# Revit family: Indoor_Pendant Lamp_Santa&Cole_La Colilla
name_source: partatom
category: Luminarias
revit_build: Autodesk Revit 2018 (Build: 20190510_1515(x64)
units: mm (PartAtom-declared; Revit-internal decimal feet)

## family parameters
Anfitrión = Cara
Compartido = No
Corte con vacíos al cargar = No
Cota de conector redondo = Diámetro de uso
Origen de luz = Sí
Punto de cálculo de habitación = No
Tipo de pieza = Normal

## types (2) — shared parameters
Assembly Instructions - CE = https://www.santacole.com
Cambio de temperatura de color de luz atenuada = <Ninguno>
Carga aparente = 6 W
Code = COL01
Elevación por defecto = 1219 mm
Energy Label = https://www.santacole.com
Fabricante = Santa & Cole
Filtro de color = 16777215
Load = 6 W
Longitud de línea de emisión = 2004 mm  [stored 6.5748 ft]
Manufacturer website = http://www.santacole.com
Modelo = La Colilla
Tamaño de símbolo de origen de luz = 50 mm  [stored 0.164042 ft]
Technical Information = https://www.santacole.com
URL = https://www.santacole.com

## type names (no varying parameters)
- Colilla
- Arne S Domus - S&C White

note: [stored X ft] marks values corroborated as IEEE doubles in the binary element streams (Revit-internal decimal feet)

## geometry (parser evidence)
native form markers: Sweep x3
no freeform markers — native parametric forms only
